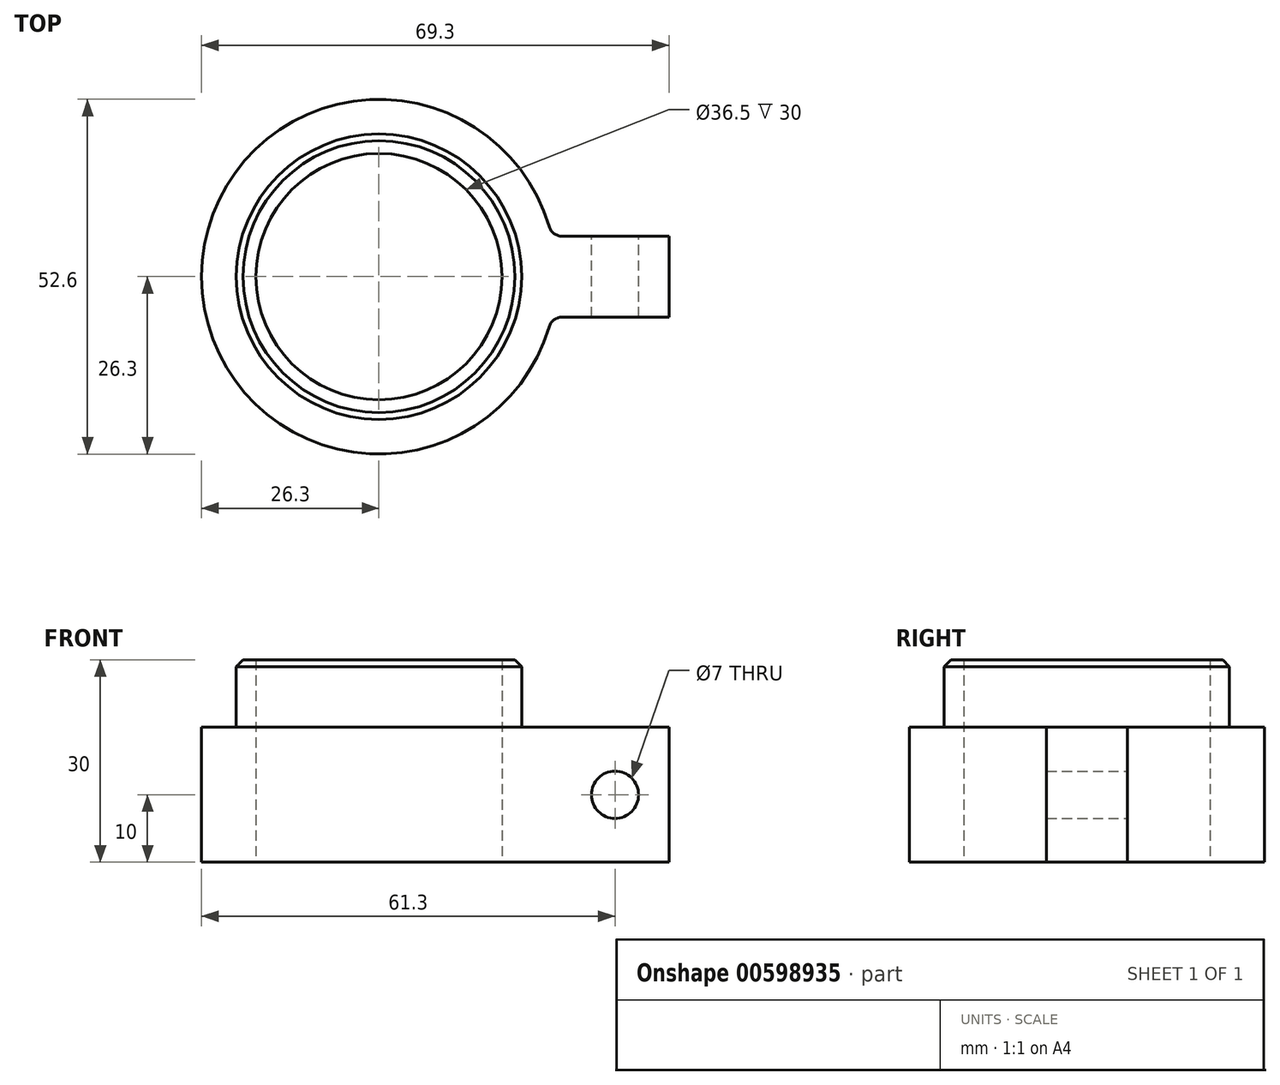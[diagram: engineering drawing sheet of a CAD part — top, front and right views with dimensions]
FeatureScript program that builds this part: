
annotation { "Feature Type Name" : "Feature", "Feature Type Description" : "" }
export const myFeature = defineFeature(function(context is Context, id is Id, definition is map)
    precondition{}
    {
        {
            var Q0;
            Q0=qCreatedBy(makeId("Front.planeOp"),FACE);
            var sketch = newSketch(context, id + "F0", { "sketchPlane" : qUnion([Q0])});
            skLineSegment(sketch, "E0", {"start": v(0, 0) * mm, "end": v(0, 45) * mm, "construction": true});
            skLineSegment(sketch, "E1", {"start": v(0, 30) * mm, "end": v(21.15, 30) * mm});
            skLineSegment(sketch, "E2", {"start": v(21.15, 30) * mm, "end": v(21.15, 20) * mm});
            skLineSegment(sketch, "E3", {"start": v(21.15, 20) * mm, "end": v(26.3, 20) * mm});
            skLineSegment(sketch, "E4", {"start": v(26.3, 20) * mm, "end": v(26.3, 0) * mm});
            skLineSegment(sketch, "E5", {"start": v(26.3, 0) * mm, "end": v(0, 0) * mm});
            skLineSegment(sketch, "E6", {"start": v(0, 30) * mm, "end": v(0, 0) * mm});
            skSolve(sketch);
        }
        {
            var Q0;
            Q0 = qSketchRegion(id + "F0", true);
            var Q1;
            Q1=sQuery(id+"F0.wireOp",EDGE,"E0");
            revolve(context, id + "F1", {"entities" : qUnion([Q0]), "axis" : qUnion([Q1]), "revolveType" : RevolveType.FULL});
        }
        {
            var Q0;
            Q0=qCreatedBy(makeId("Front.planeOp"),FACE);
            var sketch = newSketch(context, id + "F2", { "sketchPlane" : qUnion([Q0])});
            skLineSegment(sketch, "E7.bottom", {"start": v(0, 0) * mm, "end": v(43, 0) * mm});
            skLineSegment(sketch, "E7.top", {"start": v(0, 20) * mm, "end": v(43, 20) * mm});
            skLineSegment(sketch, "E7.left", {"start": v(0, 0) * mm, "end": v(0, 20) * mm});
            skLineSegment(sketch, "E7.right", {"start": v(43, 0) * mm, "end": v(43, 20) * mm});
            skCircle(sketch, "E8", {"center": v(35, 10) * mm, "radius": 3.5 * mm});
            skSolve(sketch);
        }
        {
            var Q0;
            Q0=makeQuery(id+"F2.imprint","IMPRINT",FACE,{"disambiguationData":[TD([[makeQuery(id+"F2.imprint","IMPRINT",EDGE,{"derivedFrom":sQuery(id+"F2.wireOp",EDGE,"E7.bottom")}),1.0]])]});
            extrude(context, id + "F3", {"entities" : qUnion([Q0]), "operationType" : NewBodyOperationType.ADD, "endBound" : BoundingType.SYMMETRIC, "depth" : 12 * mm, "offsetDistance" : 25 * mm, "hasSecondDirection" : true, "secondDirectionOppositeDirection" : true, "secondDirectionDepth" : 25 * mm});
        }
        {
            var Q0;
            Q0=qCreatedBy(makeId("Top.planeOp"),FACE);
            var sketch = newSketch(context, id + "F4", { "sketchPlane" : qUnion([Q0])});
            skCircle(sketch, "E9", {"center": v(0, 0) * mm, "radius": 18.25 * mm});
            skSolve(sketch);
        }
        {
            var Q0;
            Q0 = qSketchRegion(id + "F4", true);
            extrude(context, id + "F5", {"entities" : qUnion([Q0]), "operationType" : NewBodyOperationType.REMOVE, "endBound" : BoundingType.THROUGH_ALL, "depth" : 25 * mm, "offsetDistance" : 25 * mm});
        }
        {
            var Q0;
            Q0=makeQuery(id+"F1.opRevolve","SWEPT_EDGE",EDGE,{"disambiguationData":[OSD([sQuery(id+"F0.wireOp",EDGE,"E1"),sQuery(id+"F0.wireOp",EDGE,"E2")])]});
            chamfer(context, id + "F6", {"entities" : qUnion([Q0]), "width" : 1 * mm, "tangentPropagation" : true});
        }
        {
            var Q0;
            Q0=makeQuery(id+"F3.boolean.opBoolean","INTERSECT",EDGE,{"derivedFrom":[makeQuery(id+"F1.opRevolve","SWEPT_FACE",FACE,{"disambiguationData":[OSD([sQuery(id+"F0.wireOp",EDGE,"E4")])]}),makeQuery(id+"F3.opExtrude","CAP_FACE",FACE,{"disambiguationData":[OSD([sQuery(id+"F2.wireOp",EDGE,"E7.bottom"),sQuery(id+"F2.wireOp",EDGE,"E7.top"),sQuery(id+"F2.wireOp",EDGE,"E7.left"),sQuery(id+"F2.wireOp",EDGE,"E7.right"),sQuery(id+"F2.wireOp",EDGE,"E8")])],"isStart":false})]});
            var Q1;
            {var subQ0=sQuery(id+"F2.wireOp",EDGE,"E8");var subQ1=sQuery(id+"F2.wireOp",EDGE,"E7.right");var subQ2=sQuery(id+"F2.wireOp",EDGE,"E7.left");var subQ3=sQuery(id+"F2.wireOp",EDGE,"E7.top");var subQ4=sQuery(id+"F2.wireOp",EDGE,"E7.bottom");Q1=makeQuery(id+"FPhZ4LjqGbFMyBG_1.2.F3.boolean.opBoolean","INTERSECT",EDGE,{"derivedFrom":[makeQuery(id+"FPhZ4LjqGbFMyBG_1.1.F3.boolean.opBoolean","SPLIT",FACE,{"disambiguationData":[TD([makeQuery(id+"F3.opExtrude","CAP_FACE",FACE,{"disambiguationData":[OSD([subQ4,subQ3,subQ2,subQ1,subQ0])],"isStart":false})])],"derivedFrom":makeQuery(id+"F1.opRevolve","SWEPT_FACE",FACE,{"disambiguationData":[OSD([sQuery(id+"F0.wireOp",EDGE,"E4")])]})}),makeQuery(id+"FPhZ4LjqGbFMyBG_1.2.F3.opExtrude","CAP_FACE",FACE,{"disambiguationData":[OSD([subQ4,subQ3,subQ2,subQ1,subQ0])],"isStart":true})]});}
            var Q2;
            {var subQ0=sQuery(id+"F2.wireOp",EDGE,"E8");var subQ1=sQuery(id+"F2.wireOp",EDGE,"E7.right");var subQ2=sQuery(id+"F2.wireOp",EDGE,"E7.left");var subQ3=sQuery(id+"F2.wireOp",EDGE,"E7.top");var subQ4=sQuery(id+"F2.wireOp",EDGE,"E7.bottom");Q2=makeQuery(id+"FPhZ4LjqGbFMyBG_1.2.F3.boolean.opBoolean","INTERSECT",EDGE,{"derivedFrom":[makeQuery(id+"FPhZ4LjqGbFMyBG_1.1.F3.boolean.opBoolean","SPLIT",FACE,{"disambiguationData":[TD([makeQuery(id+"F3.opExtrude","CAP_FACE",FACE,{"disambiguationData":[OSD([subQ4,subQ3,subQ2,subQ1,subQ0])],"isStart":false})])],"derivedFrom":makeQuery(id+"F1.opRevolve","SWEPT_FACE",FACE,{"disambiguationData":[OSD([sQuery(id+"F0.wireOp",EDGE,"E4")])]})}),makeQuery(id+"FPhZ4LjqGbFMyBG_1.2.F3.opExtrude","CAP_FACE",FACE,{"disambiguationData":[OSD([subQ4,subQ3,subQ2,subQ1,subQ0])],"isStart":false})]});}
            var Q3;
            Q3=makeQuery(id+"FPhZ4LjqGbFMyBG_1.1.F3.boolean.opBoolean","INTERSECT",EDGE,{"derivedFrom":[makeQuery(id+"F1.opRevolve","SWEPT_FACE",FACE,{"disambiguationData":[OSD([sQuery(id+"F0.wireOp",EDGE,"E4")])]}),makeQuery(id+"FPhZ4LjqGbFMyBG_1.1.F3.opExtrude","CAP_FACE",FACE,{"disambiguationData":[OSD([sQuery(id+"F2.wireOp",EDGE,"E7.bottom"),sQuery(id+"F2.wireOp",EDGE,"E7.top"),sQuery(id+"F2.wireOp",EDGE,"E7.left"),sQuery(id+"F2.wireOp",EDGE,"E7.right"),sQuery(id+"F2.wireOp",EDGE,"E8")])],"isStart":true})]});
            var Q4;
            Q4=makeQuery(id+"FPhZ4LjqGbFMyBG_1.1.F3.boolean.opBoolean","INTERSECT",EDGE,{"derivedFrom":[makeQuery(id+"F1.opRevolve","SWEPT_FACE",FACE,{"disambiguationData":[OSD([sQuery(id+"F0.wireOp",EDGE,"E4")])]}),makeQuery(id+"FPhZ4LjqGbFMyBG_1.1.F3.opExtrude","CAP_FACE",FACE,{"disambiguationData":[OSD([sQuery(id+"F2.wireOp",EDGE,"E7.bottom"),sQuery(id+"F2.wireOp",EDGE,"E7.top"),sQuery(id+"F2.wireOp",EDGE,"E7.left"),sQuery(id+"F2.wireOp",EDGE,"E7.right"),sQuery(id+"F2.wireOp",EDGE,"E8")])],"isStart":false})]});
            var Q5;
            Q5=makeQuery(id+"F3.boolean.opBoolean","INTERSECT",EDGE,{"derivedFrom":[makeQuery(id+"F1.opRevolve","SWEPT_FACE",FACE,{"disambiguationData":[OSD([sQuery(id+"F0.wireOp",EDGE,"E4")])]}),makeQuery(id+"F3.opExtrude","CAP_FACE",FACE,{"disambiguationData":[OSD([sQuery(id+"F2.wireOp",EDGE,"E7.bottom"),sQuery(id+"F2.wireOp",EDGE,"E7.top"),sQuery(id+"F2.wireOp",EDGE,"E7.left"),sQuery(id+"F2.wireOp",EDGE,"E7.right"),sQuery(id+"F2.wireOp",EDGE,"E8")])],"isStart":true})]});
            fillet(context, id + "F7", {"entities" : qUnion([Q0, Q1, Q2, Q3, Q4, Q5]), "radius" : 2 * mm, "tangentPropagation" : true, "allowEdgeOverflow" : false});
        }
    });
